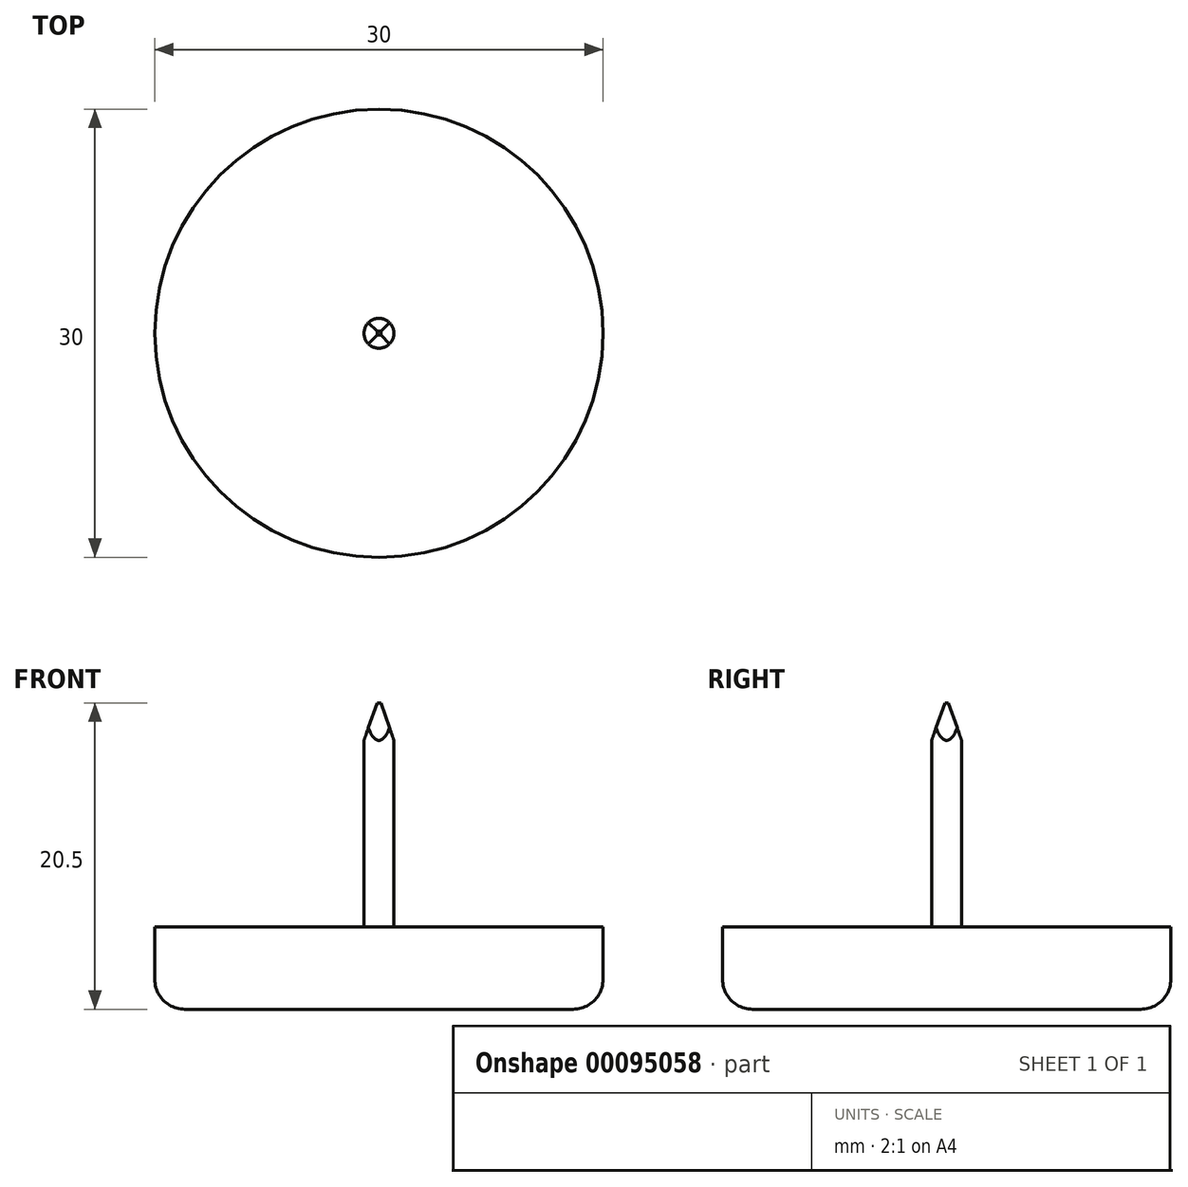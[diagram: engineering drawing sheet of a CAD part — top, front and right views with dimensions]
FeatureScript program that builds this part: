
annotation { "Feature Type Name" : "Feature", "Feature Type Description" : "" }
export const myFeature = defineFeature(function(context is Context, id is Id, definition is map)
    precondition{}
    {
        {
            var Q0;
            Q0=qCreatedBy(makeId("Top.planeOp"),FACE);
            var sketch = newSketch(context, id + "F0", { "sketchPlane" : qUnion([Q0])});
            skCircle(sketch, "E0", {"center": v(0, 0) * mm, "radius": 15 * mm});
            skSolve(sketch);
        }
        {
            var Q0;
            Q0 = qSketchRegion(id + "F0", true);
            extrude(context, id + "F1", {"entities" : qUnion([Q0]), "depth" : 5.5 * mm});
        }
        {
            var Q0;
            Q0=makeQuery(id+"F1.opExtrude","CAP_EDGE",EDGE,{"disambiguationData":[OSD([sQuery(id+"F0.wireOp",EDGE,"E0")])],"isStart":true});
            fillet(context, id + "F2", {"entities" : qUnion([Q0]), "radius" : 2 * mm, "tangentPropagation" : true, "allowEdgeOverflow" : false});
        }
        {
            var Q0;
            Q0=makeQuery(id+"F1.opExtrude","CAP_FACE",FACE,{"disambiguationData":[OSD([sQuery(id+"F0.wireOp",EDGE,"E0")])],"isStart":false});
            var sketch = newSketch(context, id + "F3", { "sketchPlane" : qUnion([Q0])});
            skCircle(sketch, "E1", {"center": v(0, 0) * mm, "radius": 1 * mm});
            skSolve(sketch);
        }
        {
            var Q0;
            Q0 = qSketchRegion(id + "F3", true);
            extrude(context, id + "F4", {"entities" : qUnion([Q0]), "operationType" : NewBodyOperationType.ADD, "depth" : 15 * mm});
        }
        {
            var Q0;
            Q0=qCreatedBy(makeId("Front.planeOp"),FACE);
            var sketch = newSketch(context, id + "F5", { "sketchPlane" : qUnion([Q0])});
            skLineSegment(sketch, "E2.0", {"start": v(-1, 20.5) * mm, "end": v(1, 20.5) * mm});
            skLineSegment(sketch, "E3", {"start": v(-1, 20.5) * mm, "end": v(-1, 18) * mm});
            skLineSegment(sketch, "E4", {"start": v(-1, 18) * mm, "end": v(-0.12, 20.5) * mm});
            skLineSegment(sketch, "E5", {"start": v(0.12, 20.5) * mm, "end": v(1, 18) * mm});
            skLineSegment(sketch, "E6", {"start": v(1, 18) * mm, "end": v(1, 20.5) * mm});
            skLineSegment(sketch, "E7", {"start": v(0, 20.5) * mm, "end": v(0, 18) * mm, "construction": true});
            skSolve(sketch);
        }
        {
            var Q0;
            Q0 = qSketchRegion(id + "F5", true);
            extrude(context, id + "F6", {"entities" : qUnion([Q0]), "operationType" : NewBodyOperationType.REMOVE, "endBound" : BoundingType.THROUGH_ALL, "oppositeDirection" : true, "depth" : 25 * mm, "hasSecondDirection" : true, "secondDirectionBound" : SecondDirectionBoundingType.THROUGH_ALL, "secondDirectionOppositeDirection" : false, "secondDirectionDepth" : 25 * mm});
        }
        {
            var Q0;
            Q0=qCreatedBy(makeId("Right.planeOp"),FACE);
            var sketch = newSketch(context, id + "F7", { "sketchPlane" : qUnion([Q0])});
            skLineSegment(sketch, "E8.0", {"start": v(-1, 20.5) * mm, "end": v(-1, 20.5) * mm});
            skLineSegment(sketch, "E9.0", {"start": v(1, 20.5) * mm, "end": v(0.13, 20.5) * mm});
            skLineSegment(sketch, "E9.1", {"start": v(1, 20.5) * mm, "end": v(1, 20.5) * mm});
            skLineSegment(sketch, "E10", {"start": v(1, 20.5) * mm, "end": v(1, 18) * mm});
            skLineSegment(sketch, "E11", {"start": v(1, 18) * mm, "end": v(0.12, 20.5) * mm});
            skLineSegment(sketch, "E12", {"start": v(-1, 20.5) * mm, "end": v(-1, 18) * mm});
            skLineSegment(sketch, "E13", {"start": v(-1, 18) * mm, "end": v(-0.13, 20.5) * mm});
            skLineSegment(sketch, "E14.trimOffspring", {"start": v(-0.12, 20.5) * mm, "end": v(-1, 20.5) * mm});
            skSolve(sketch);
        }
        {
            var Q0;
            Q0 = qSketchRegion(id + "F7", true);
            extrude(context, id + "F8", {"entities" : qUnion([Q0]), "operationType" : NewBodyOperationType.REMOVE, "endBound" : BoundingType.THROUGH_ALL, "depth" : 25 * mm, "hasSecondDirection" : true, "secondDirectionBound" : SecondDirectionBoundingType.THROUGH_ALL, "secondDirectionOppositeDirection" : true, "secondDirectionDepth" : 25 * mm});
        }
    });
